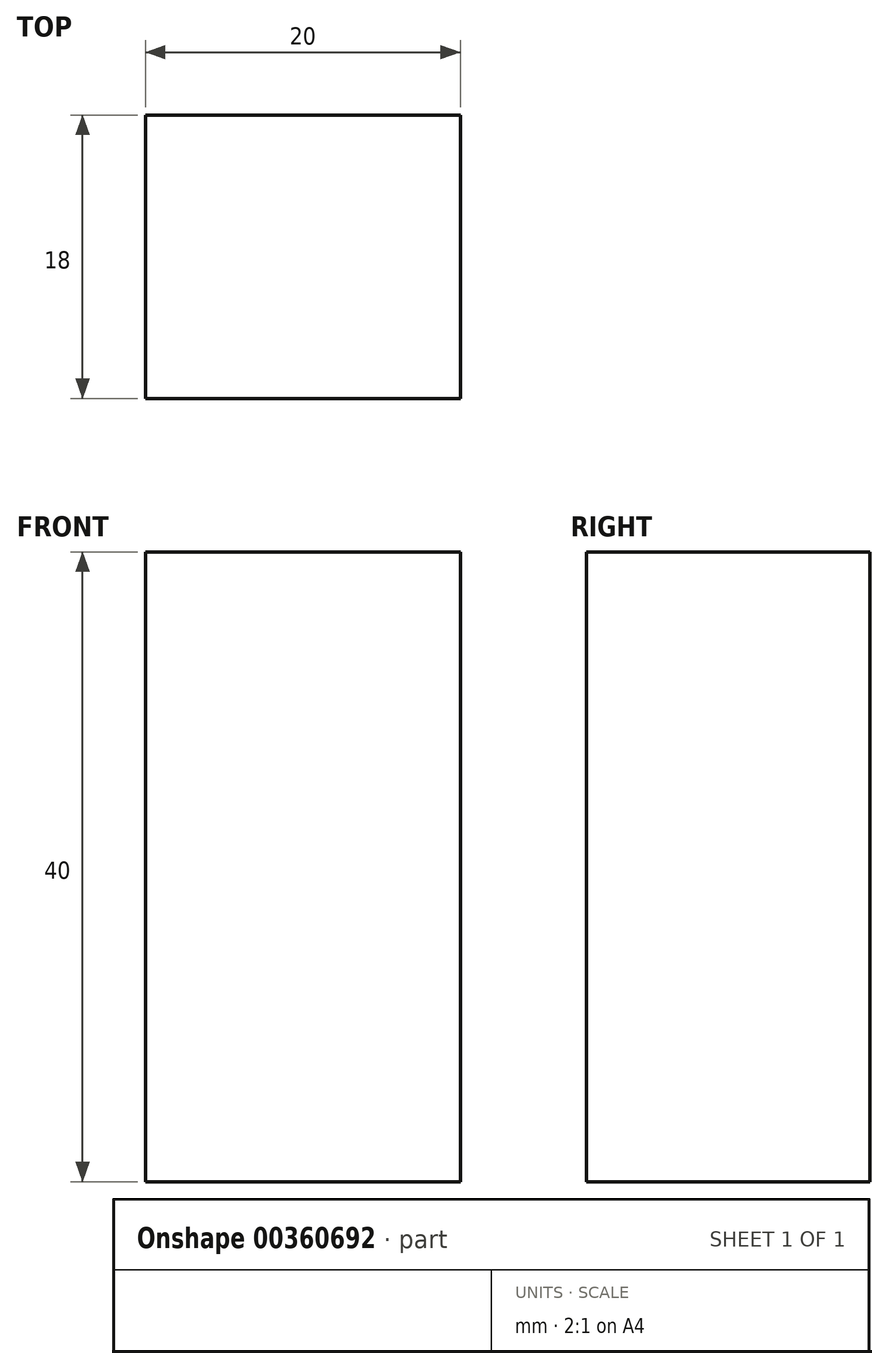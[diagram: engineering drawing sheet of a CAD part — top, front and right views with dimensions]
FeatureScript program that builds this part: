
annotation { "Feature Type Name" : "Feature", "Feature Type Description" : "" }
export const myFeature = defineFeature(function(context is Context, id is Id, definition is map)
    precondition{}
    {
        {
            var Q0;
            Q0=qCreatedBy(makeId("Front.planeOp"),FACE);
            var sketch = newSketch(context, id + "F0", { "sketchPlane" : qUnion([Q0])});
            skLineSegment(sketch, "E0.bottom", {"start": v(0, 0) * mm, "end": v(20, 0) * mm});
            skLineSegment(sketch, "E0.top", {"start": v(0, 40) * mm, "end": v(20, 40) * mm});
            skLineSegment(sketch, "E0.left", {"start": v(0, 0) * mm, "end": v(0, 40) * mm});
            skLineSegment(sketch, "E0.right", {"start": v(20, 0) * mm, "end": v(20, 40) * mm});
            skSolve(sketch);
        }
        {
            var Q0;
            Q0=makeQuery(id+"F0.imprint","IMPRINT",FACE,{"disambiguationData":[TD([[makeQuery(id+"F0.imprint","IMPRINT",EDGE,{"derivedFrom":sQuery(id+"F0.wireOp",EDGE,"E0.bottom")}),1.0]])]});
            extrude(context, id + "F1", {"entities" : qUnion([Q0]), "depth" : 18 * mm});
        }
    });
